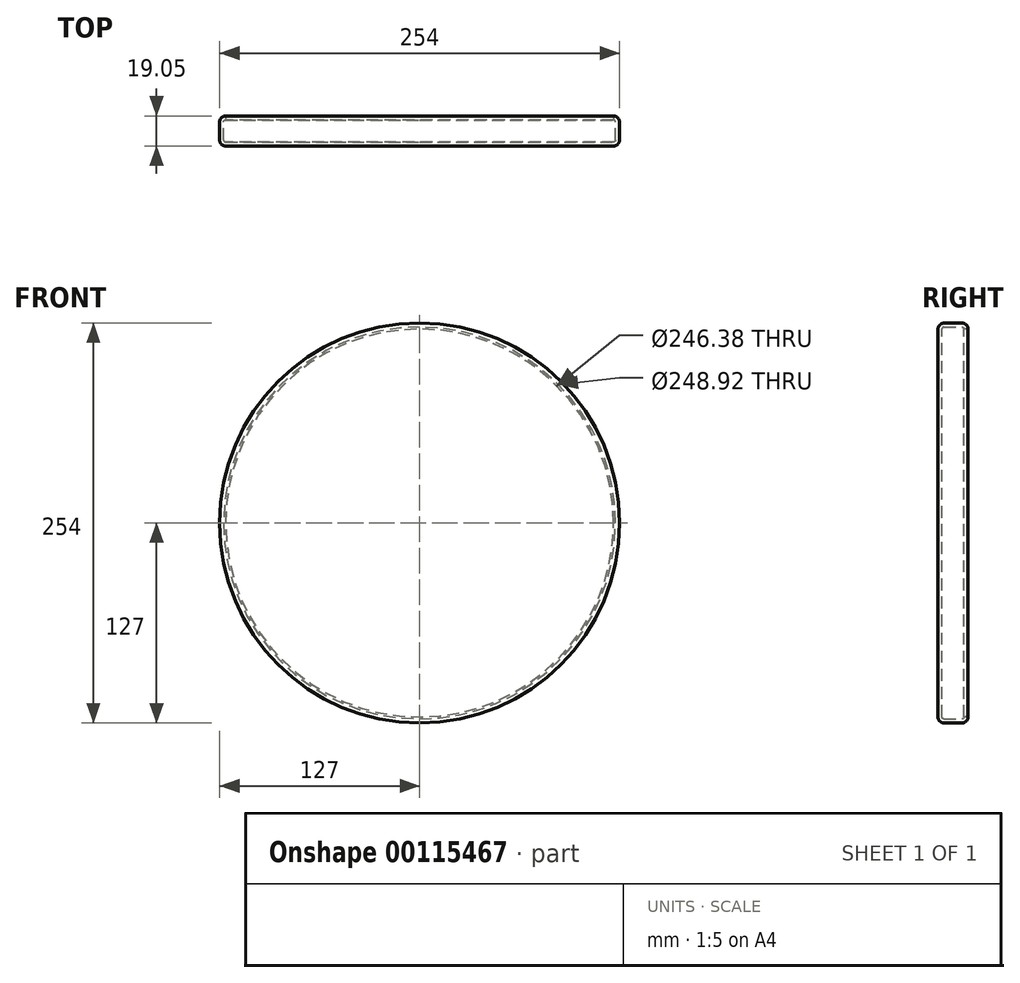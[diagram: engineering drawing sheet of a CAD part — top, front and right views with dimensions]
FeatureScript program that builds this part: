
annotation { "Feature Type Name" : "Feature", "Feature Type Description" : "" }
export const myFeature = defineFeature(function(context is Context, id is Id, definition is map)
    precondition{}
    {
        {
            var Q0;
            Q0=qCreatedBy(makeId("Front.planeOp"),FACE);
            var sketch = newSketch(context, id + "F0", { "sketchPlane" : qUnion([Q0])});
            skCircle(sketch, "E0", {"center": v(0, 0) * mm, "radius": 127 * mm});
            skSolve(sketch);
        }
        {
            var Q0;
            Q0=makeQuery(id+"F0.imprint","IMPRINT",FACE,{"disambiguationData":[TD([[makeQuery(id+"F0.imprint","IMPRINT",EDGE,{"derivedFrom":sQuery(id+"F0.wireOp",EDGE,"E0")}),1.0]])]});
            extrude(context, id + "F1", {"entities" : qUnion([Q0]), "depth" : 19.05 * mm});
        }
        {
            var Q0;
            Q0=makeQuery(id+"F1.opExtrude","CAP_EDGE",EDGE,{"disambiguationData":[OSD([sQuery(id+"F0.wireOp",EDGE,"E0")])],"isStart":true});
            var Q1;
            Q1=makeQuery(id+"F1.opExtrude","CAP_EDGE",EDGE,{"disambiguationData":[OSD([sQuery(id+"F0.wireOp",EDGE,"E0")])],"isStart":false});
            fillet(context, id + "F2", {"entities" : qUnion([Q0, Q1]), "radius" : 3.8 * mm, "tangentPropagation" : true, "allowEdgeOverflow" : false});
        }
        {
            var Q0;
            Q0=makeQuery(id+"F1.opExtrude","CAP_FACE",FACE,{"disambiguationData":[OSD([sQuery(id+"F0.wireOp",EDGE,"E0")])],"isStart":true});
            shell(context, id + "F3", {"entities" : qUnion([Q0]), "thickness" : 2.54 * mm});
        }
    });
